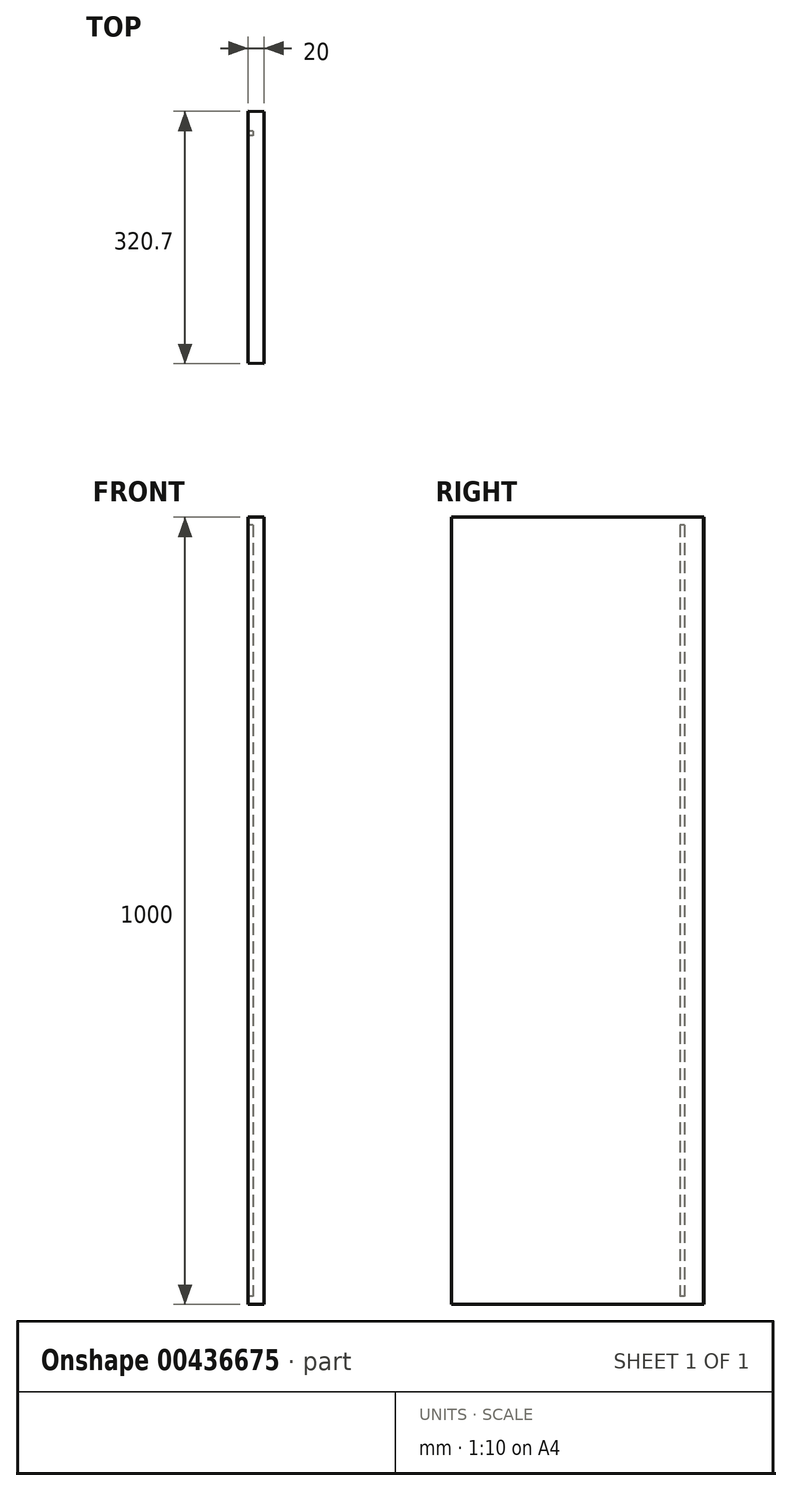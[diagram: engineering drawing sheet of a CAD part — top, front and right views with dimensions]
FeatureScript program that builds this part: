
annotation { "Feature Type Name" : "Feature", "Feature Type Description" : "" }
export const myFeature = defineFeature(function(context is Context, id is Id, definition is map)
    precondition{}
    {
        {
            var Q0;
            Q0=qCreatedBy(makeId("Top.planeOp"),FACE);
            var sketch = newSketch(context, id + "F0", { "sketchPlane" : qUnion([Q0])});
            skLineSegment(sketch, "E0.left", {"start": v(-13.06, 132.1) * mm, "end": v(-13.06, -187.9) * mm});
            skLineSegment(sketch, "E0.right", {"start": v(-33.06, 132.79) * mm, "end": v(-33.06, -187.21) * mm});
            skPoint(sketch, "E0.middle", {"position": v(0, 0) * mm});
            skLineSegment(sketch, "E1", {"start": v(-13.06, -187.9) * mm, "end": v(-33.06, -187.21) * mm});
            skLineSegment(sketch, "E2", {"start": v(-13.06, 132.1) * mm, "end": v(-33.06, 132.79) * mm});
            skSolve(sketch);
        }
        {
            var Q0;
            Q0 = qSketchRegion(id + "F0", true);
            extrude(context, id + "F1", {"entities" : qUnion([Q0]), "depth" : 1000 * mm});
        }
        {
            var Q0;
            Q0=makeQuery(id+"F1.opExtrude","SWEPT_FACE",FACE,{"disambiguationData":[OSD([sQuery(id+"F0.wireOp",EDGE,"E0.right")])]});
            var sketch = newSketch(context, id + "F2", { "sketchPlane" : qUnion([Q0])});
            skLineSegment(sketch, "E3.bottom", {"start": v(-107.79, 990) * mm, "end": v(-101.79, 990) * mm});
            skLineSegment(sketch, "E3.top", {"start": v(-107.79, 10) * mm, "end": v(-101.79, 10) * mm});
            skLineSegment(sketch, "E3.left", {"start": v(-107.79, 990) * mm, "end": v(-107.79, 10) * mm});
            skLineSegment(sketch, "E3.right", {"start": v(-101.79, 990) * mm, "end": v(-101.79, 10) * mm});
            skSolve(sketch);
        }
        {
            var Q0;
            Q0 = qSketchRegion(id + "F2", true);
            extrude(context, id + "F3", {"entities" : qUnion([Q0]), "operationType" : NewBodyOperationType.REMOVE, "oppositeDirection" : true, "depth" : 6 * mm});
        }
    });
